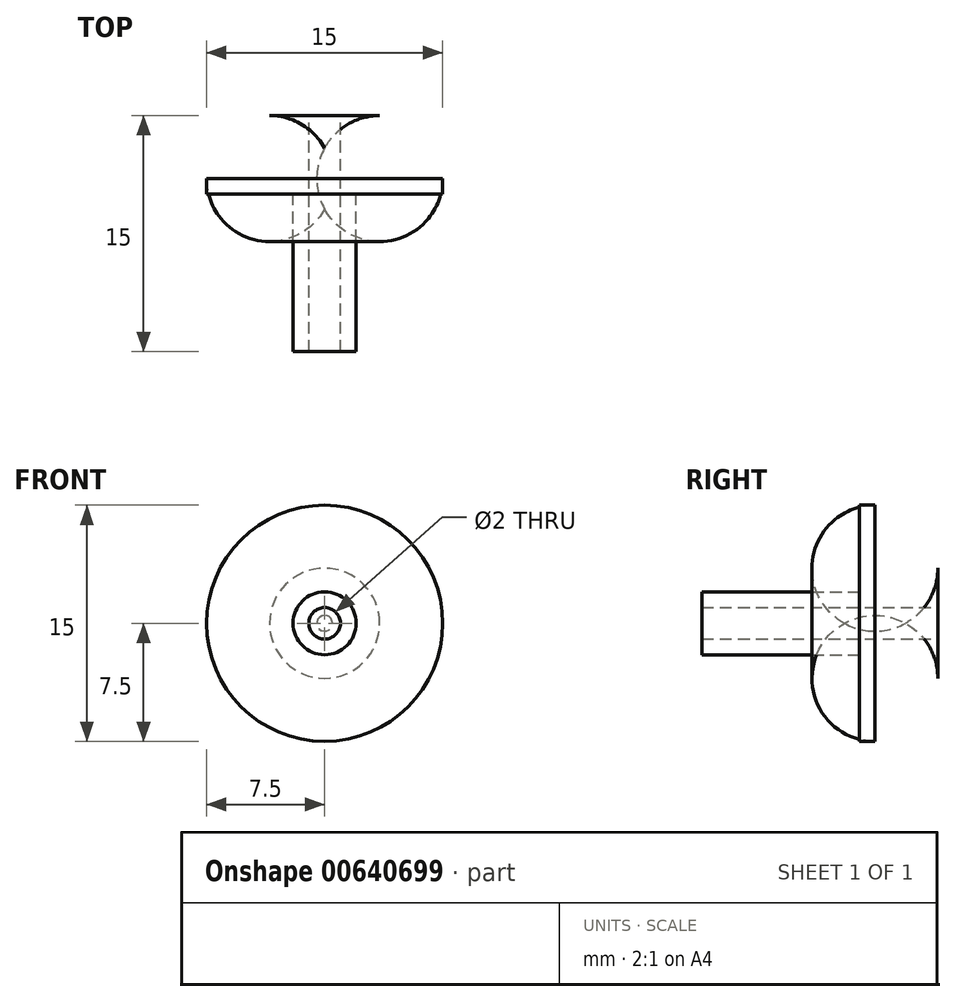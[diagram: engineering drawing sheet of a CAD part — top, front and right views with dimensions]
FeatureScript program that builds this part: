
annotation { "Feature Type Name" : "Feature", "Feature Type Description" : "" }
export const myFeature = defineFeature(function(context is Context, id is Id, definition is map)
    precondition{}
    {
        {
            var Q0;
            Q0=qCreatedBy(makeId("Front.planeOp"),FACE);
            var sketch = newSketch(context, id + "F0", { "sketchPlane" : qUnion([Q0])});
            skCircle(sketch, "E0", {"center": v(0, 0) * mm, "radius": 2 * mm});
            skCircle(sketch, "E1", {"center": v(0, 0) * mm, "radius": 1 * mm});
            skSolve(sketch);
        }
        {
            var Q0;
            Q0=makeQuery(id+"F0.imprint","IMPRINT",FACE,{"disambiguationData":[TD([[makeQuery(id+"F0.imprint","IMPRINT",EDGE,{"derivedFrom":sQuery(id+"F0.wireOp",EDGE,"E0")}),1.0]])]});
            extrude(context, id + "F1", {"entities" : qUnion([Q0]), "depth" : 10 * mm, "offsetDistance" : 25 * mm});
        }
        {
            var Q0;
            Q0=qCreatedBy(makeId("Front.planeOp"),FACE);
            var sketch = newSketch(context, id + "F2", { "sketchPlane" : qUnion([Q0])});
            skCircle(sketch, "E2", {"center": v(0, 0) * mm, "radius": 7.5 * mm});
            skSolve(sketch);
        }
        {
            var Q0;
            Q0 = qSketchRegion(id + "F2", true);
            extrude(context, id + "F3", {"entities" : qUnion([Q0]), "operationType" : NewBodyOperationType.ADD, "oppositeDirection" : true, "depth" : 5 * mm, "offsetDistance" : 25 * mm});
        }
        {
            var Q0;
            Q0=makeQuery(id+"F3.opExtrude","CAP_FACE",FACE,{"disambiguationData":[OSD([sQuery(id+"F2.wireOp",EDGE,"E2")])],"isStart":false});
            var sketch = newSketch(context, id + "F4", { "sketchPlane" : qUnion([Q0])});
            skCircle(sketch, "E3", {"center": v(0, 0) * mm, "radius": 1 * mm});
            skSolve(sketch);
        }
        {
            var Q0;
            Q0 = qSketchRegion(id + "F4", true);
            extrude(context, id + "F5", {"entities" : qUnion([Q0]), "operationType" : NewBodyOperationType.REMOVE, "endBound" : BoundingType.THROUGH_ALL, "oppositeDirection" : true, "depth" : 25 * mm, "offsetDistance" : 25 * mm});
        }
        {
            var Q0;
            Q0=makeQuery(id+"F3.opExtrude","CAP_EDGE",EDGE,{"disambiguationData":[OSD([sQuery(id+"F2.wireOp",EDGE,"E2")])],"isStart":false});
            fillet(context, id + "F6", {"entities" : qUnion([Q0]), "radius" : 4 * mm, "tangentPropagation" : true, "allowEdgeOverflow" : false});
        }
    });
